# Revit family: EN 200 ATJ STV
name_source: partatom
category: Equipement spécialisé
units: mm (PartAtom-declared; Revit-internal decimal feet)

## family parameters
Basée sur le plan de construction = Non
Cote de connecteur circulaire = Utiliser le diamètre
Couper avec des vides une fois chargée = Non
Numéro OmniClass = 23.50.00.00
Partagée = Non
Point de calcul de pièce = Non
Titre OmniClass = Conveying Systems & Material Handling
Toujours verticalement = Oui
Type d'élément = Normal

## types (1)
- 200 ATJ RC ST5 S1
    Average consumption (L/h) = 1.718
    Average consumption (l/day) = 0.00 m
    CO2 emissions (g/kWh) = 4.5
    Counterweight offset (turret at 90°) = 115.00 m
    Créé par = ATLANCAD
    Description = Nacelle 3 bras
    Elévation par défaut = 0.00 m
    Engine norm = A préciser
    External turning radius = 3.90 m
    Fabricant = MANITOU
    Floor height (access) = 18.35 m
    Ground clearance = 0.45 m
    Ground clearance at centre of wheelbase = 0.45 m
    I.C. Engine power rating - Power (ch) = 34
    I.C. Engine power rating - Power (kW) = 25.5
    Internal turning radius (over tyres) = 1.26 m
    Jib length = 2.00 m
    Masse à vide du panier = 187.00 kg
    Max. lifting height = 18.35 m
    Max. outreach = 11.97 m
    Modèle = 200 ATJ RC ST5 S1
    Noise to environment (LwA) = 107
    Number of people (inside) = 2
    Number of people (outside) = 2
    Overall height (stowed) = 2.99 m
    Overall height (transport) = 2.70 m
    Overall lenght (stowed) = 8.43 m
    Overall lenght (transport) = 6.24 m
    Overhang = 7.96 m
    Permissible leveling = 5.00°
    Platform capacity = 230.00 kg
    Platform dimensions (length) = 2.06 m
    Platform dimensions (width) = 0.68 m
    Platform weight = 10050.00 kg
    URL = www.manitou.com
    Wheelbase = 2.41 m
    Width = 2.49 m
